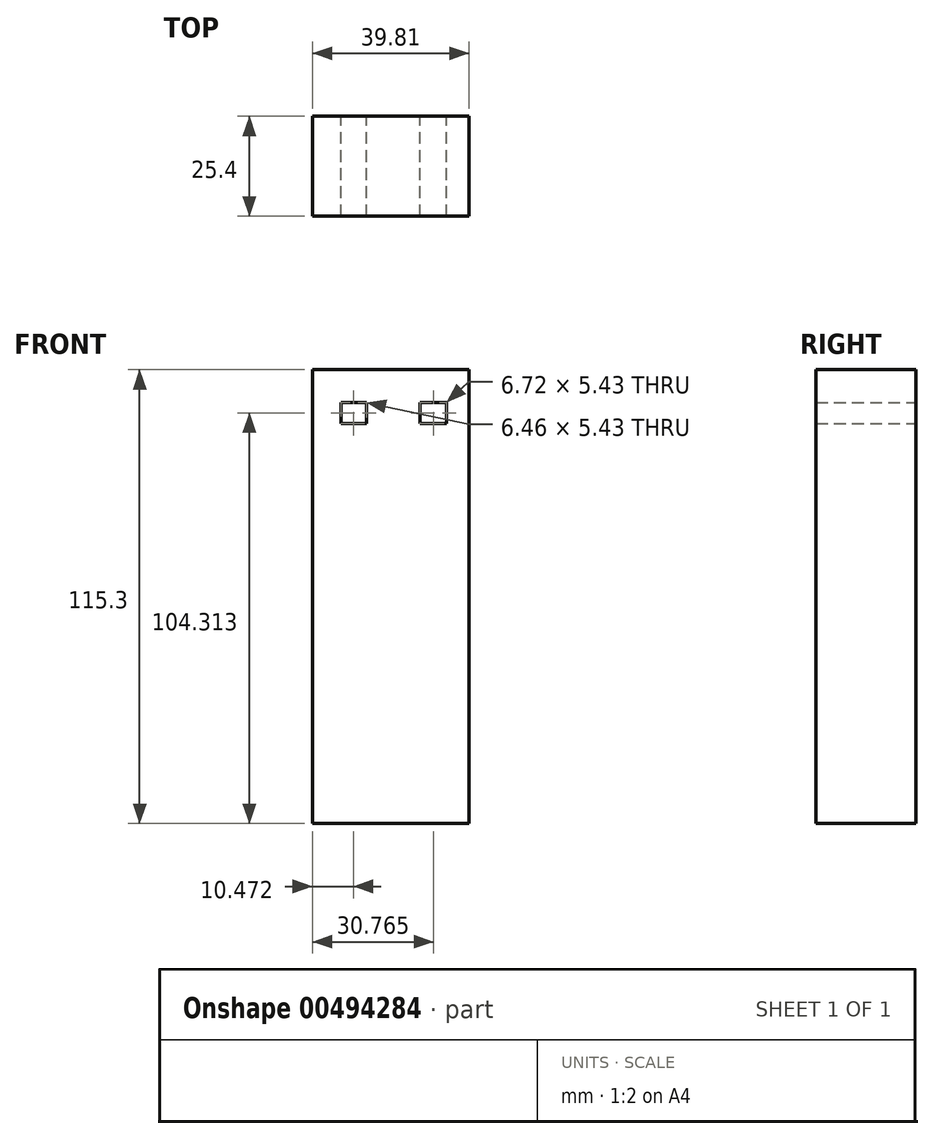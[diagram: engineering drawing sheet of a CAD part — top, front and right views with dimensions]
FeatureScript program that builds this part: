
annotation { "Feature Type Name" : "Feature", "Feature Type Description" : "" }
export const myFeature = defineFeature(function(context is Context, id is Id, definition is map)
    precondition{}
    {
        {
            var Q0;
            Q0=qCreatedBy(makeId("Front.planeOp"),FACE);
            var sketch = newSketch(context, id + "F0", { "sketchPlane" : qUnion([Q0])});
            skLineSegment(sketch, "E0.bottom", {"start": v(-23, 43.56) * mm, "end": v(16.8, 43.56) * mm});
            skLineSegment(sketch, "E0.top", {"start": v(-23, -71.74) * mm, "end": v(16.8, -71.74) * mm});
            skLineSegment(sketch, "E0.left", {"start": v(-23, 43.56) * mm, "end": v(-23, -71.74) * mm});
            skLineSegment(sketch, "E0.right", {"start": v(16.8, 43.56) * mm, "end": v(16.8, -71.74) * mm});
            skLineSegment(sketch, "E1.bottom", {"start": v(-15.77, 35.29) * mm, "end": v(-9.3, 35.29) * mm});
            skLineSegment(sketch, "E1.top", {"start": v(-15.77, 29.86) * mm, "end": v(-9.3, 29.86) * mm});
            skLineSegment(sketch, "E1.left", {"start": v(-15.77, 35.29) * mm, "end": v(-15.77, 29.86) * mm});
            skLineSegment(sketch, "E1.right", {"start": v(-9.3, 35.29) * mm, "end": v(-9.3, 29.86) * mm});
            skLineSegment(sketch, "E2.bottom", {"start": v(4.4, 35.29) * mm, "end": v(11.12, 35.29) * mm});
            skLineSegment(sketch, "E2.top", {"start": v(4.4, 29.86) * mm, "end": v(11.12, 29.86) * mm});
            skLineSegment(sketch, "E2.left", {"start": v(4.4, 35.29) * mm, "end": v(4.4, 29.86) * mm});
            skLineSegment(sketch, "E2.right", {"start": v(11.12, 35.29) * mm, "end": v(11.12, 29.86) * mm});
            skSolve(sketch);
        }
        {
            var Q0;
            Q0=makeQuery(id+"F0.imprint","IMPRINT",FACE,{"disambiguationData":[TD([[makeQuery(id+"F0.imprint","IMPRINT",EDGE,{"derivedFrom":sQuery(id+"F0.wireOp",EDGE,"E0.bottom")}),-1.0]])]});
            extrude(context, id + "F1", {"entities" : qUnion([Q0]), "depth" : 25.4 * mm});
        }
    });
